# Revit family: IS_iLifeA_T5256_BIM_NL
name_source: partatom
category: Plumbing Fixtures
units: mm (PartAtom-declared; Revit-internal decimal feet)

## family parameters
Always vertical = No
Cut with Voids When Loaded = No
OmniClass Number = 23.45.05.14.21.11
OmniClass Title = Bath/Shower Units
Part Type = Normal
Room Calculation Point = No
Round Connector Dimension = Use Diameter
Shared = No
Work Plane-Based = No

## types (7) — shared parameters
Accesoires = https://www.idealstandard.de
Accessories = https://www.idealstandard.nl
Afmetingen = 800 x 460 x 630 mm
AfstandsEenheid = Millimeter
AreaUnits = milliliters
Artikelomschrijving = I.Life A Waschtischunterschrank 2 Schubladen 80cm
Auteur = Ideal Standard
BIMObjectName = IS_IdealStandard_BathroomCabinets_I.Life A_T5256
BIMobject category = Other Sanitary
BIMobject category code = other-sanitary
BIMobject main category = Sanitary
BIMobject main category code = sanitary
Beschrijvinggarantie = Herstellergarantie
BimObjectNaam = IS_IdealStandard_BathroomCabinets_I.Life A_T5256
Brand = Ideal Standard
Brand url = https://www.idealstandard.nl
Breedte = 800
ConnectionType = Plumbing
CurrencyUnit = €
CurrentRevision = 1
Date of publishing = 11/03/2022
Description = I.Life A Vanity Unit 2 Drawers 80cm
Diepte = 460 mm
DurationUnit = Years
DuurEenheid = Jahre
Edition number = 1
Eigenschappen = Waschtischunterschrank 2 Schubladen 80cm
ElementType = Bathroom Furniture
Features = Vanity Unit 2 Drawers 80cm
Garantieonderdelen = 5
Garantieunits = Jahre
GemaaktOp = 11/03/2022
Help = https://www.idealstandard.nl
Hoogte = 630
Hulp = https://www.idealstandard.nl
IFC Classification = Sanitary Terminal
IfcExportAs = IfcFurnitureType
IfcExportType = BATHROOMCABINET
Installatieinstructies = https://www.idealstandard.nl
Installation instructions = https://www.idealstandard.nl
InstallationInstructions = https://www.idealstandard.nl
Lengte = 460 mm
LinearUnits = millilitres
MaintenanceInformation = https://www.idealstandard.nl
Manufacturer = Ideal Standard
Manufacturer name = Ideal Standard
ManufacturerURL = https://www.idealstandard.nl
Masterformat 2014 Code = 12 50 00
Masterformat 2014 Description = Furniture
Materiaal = MDF
Material = Wood
Material main = MDF
Merk = Ideal Standard
ModelReference = I.Life A Vanity Unit 2 Drawers 80cm
NBS Reference Code = 45-35-72/318
NBS Reference Description = Bathroom Cabinets
Name = BathroomCabinets_I.Life A_T5256_IdealStandard
NettWeight = 30
Nettogewicht = 30
NominalDepth = 460 mm
NominalHeight = 630 mm  [stored 2.06693 ft]
NominalLength = 460 mm
NominalWidth = 800 mm  [stored 2.62467 ft]
OmniClass Code = 23-31 25 13
OmniClass Description = Bathroom Cabinets
OppervlakteEenheid = Millimeter
PredefinedType = Bathroom Furniture
Product Guid = 9605650b-2ea5-4f92-8306-0a6d7a05488b
Product SKU = T5256
Product certification = https://www.idealstandard.nl
Product data url = https://bimobject.com
Product family = I.life
Product group = Bathroom Furniture
Product name = I.Life A Vanity Unit 2 Drawers 80cm
Product url = https://www.idealstandard.nl
ProductInformation = https://www.idealstandard.nl
ProductSoort = Badezimmermöbel
Productinformatie = https://www.idealstandard.nl
QR code = http://bimobject.com
Referentie = I.Life A Vanity Unit 2 Drawers 80cm
Revisie = 1
Shape = rectangular
Size = 800 x 460 x 630 mm
Space = Internal
SpareParts = https://www.idealstandard.nl
Technical description = https://www.idealstandard.nl
Telefoonnummer = 077 355 08 08
Toepassing = Badezimmermöbel
Typeconnectie = Wand aufgehängt
UNSPSC Code = 301815
URL = https://www.idealstandard.nl
Uniclass 1.4 Code = L8241
Uniclass 1.4 Description = Bathroom cabinets
Uniclass 2.0 Code = PR-35-75-08
Uniclass 2.0 Description = Bathroom Cabinets
Uniclass 2015 Code = Pr_40_30_78_05
Uniclass 2015 Name = Bathroom furniture
Uniclass2015Beschrijving = Bathroom furniture
Uniclass2015Code = Pr_40_30_87_03
Uniclass2015Referentie = Pr_40_30_87_03
Uniclass2015Title = Bathroom cabinets
Uniclass2015Version = v1.25
Urlproducent = https://www.idealstandard.nl
ValutaEenheid = Euro
Versie = 1
Version = 1
VolumeUnits = Litres
Volumeunits = Liter
Vorm = rechteckig
WRASURL = https://www.wrasapprovals.co.uk
WarrantyDescription = manufacturer warranty
WarrantyDurationUnit = years
Wisselstukken = https://www.idealstandard.nl
Youtube clip = https://www.youtube.com
zero-valued in all types: BrutoGewicht, MaterialThickness, Vervangingskosten

## per-type parameters (varying)
| type | Afwerking | Artikelnummer | Artikelreferentie | BarCode | Color | Finish | GTIN code | Kleur | MainColor | Model | ModelNumber |
| T5256DU - I.Life A Vanity Unit 2 Drawers 80cm - Matt White | Mattweiß | T5256DU | T5256DU | 8014140501978 | Matt White | Matt White | https://8014140501978 | Mattweiß | Matt White | T5256DU | T5256DU |
| T5256NF - I.Life A Vanity Unit 2 Drawers 80cm - Sand Beige Matt | Sandbeige matt | T5256NF | T5256NF | 8014140493525 | Sand Beige Matt | Sand Beige Matt | https://8014140493525 | Sandbeige matt | Sand Beige Matt | T5256NF | T5256NF |
| T5256NG - I.Life A Vanity Unit 2 Drawers 80cm - Quartz Grey Matt | Quarzgrau matt | T5256NG | T5256NG | 8014140493532 | Quartz Grey Matt | Quartz Grey Matt | https://8014140493532 | Quarzgrau matt | Quartz Grey Matt | T5256NG | T5256NG |
| T5256NV - I.Life A Vanity Unit 2 Drawers 80cm - Carbon Grey Matt | Carbongrau Matt | T5256NV | T5256NV | 8014140493556 | Carbon Grey Matt | Carbon Grey Matt | https://8014140493556 | Carbongrau Matt | Carbon Grey Matt | T5256NV | T5256NV |
| T5256NH - I.Life A Vanity Unit 2 Drawers 80cm - Greige Matt | Greige Matt | T5256NH | T5256NH | 8014140493549 | Greige Matt | Greige Matt | https://8014140493549 | Greige Matt | Greige Matt | T5256NH | T5256NH |
| T5256NX - I.Life A Vanity Unit 2 Drawers 80cm - Natural Oak | Natürliche Eiche | T5256NX | T5256NX | 8014140501992 | Natural Oak | Natural Oak | https://8014140501992 | Natürliche Eiche | Natural Oak | T5256NX | T5256NX |
| T5256NW - I.Life A Vanity Unit 2 Drawers 80cm - Coffee Oak | Kaffee-Eiche | T5256NW | T5256NW | 8014140501985 | Coffee Oak | Coffee Oak | https://8014140501985 | Kaffee-Eiche | Coffee Oak | T5256NW | T5256NW |

note: [stored X ft] marks values corroborated as IEEE doubles in the binary element streams (Revit-internal decimal feet)

## geometry (parser evidence)
native form markers: Sweep x3
no freeform markers — native parametric forms only
